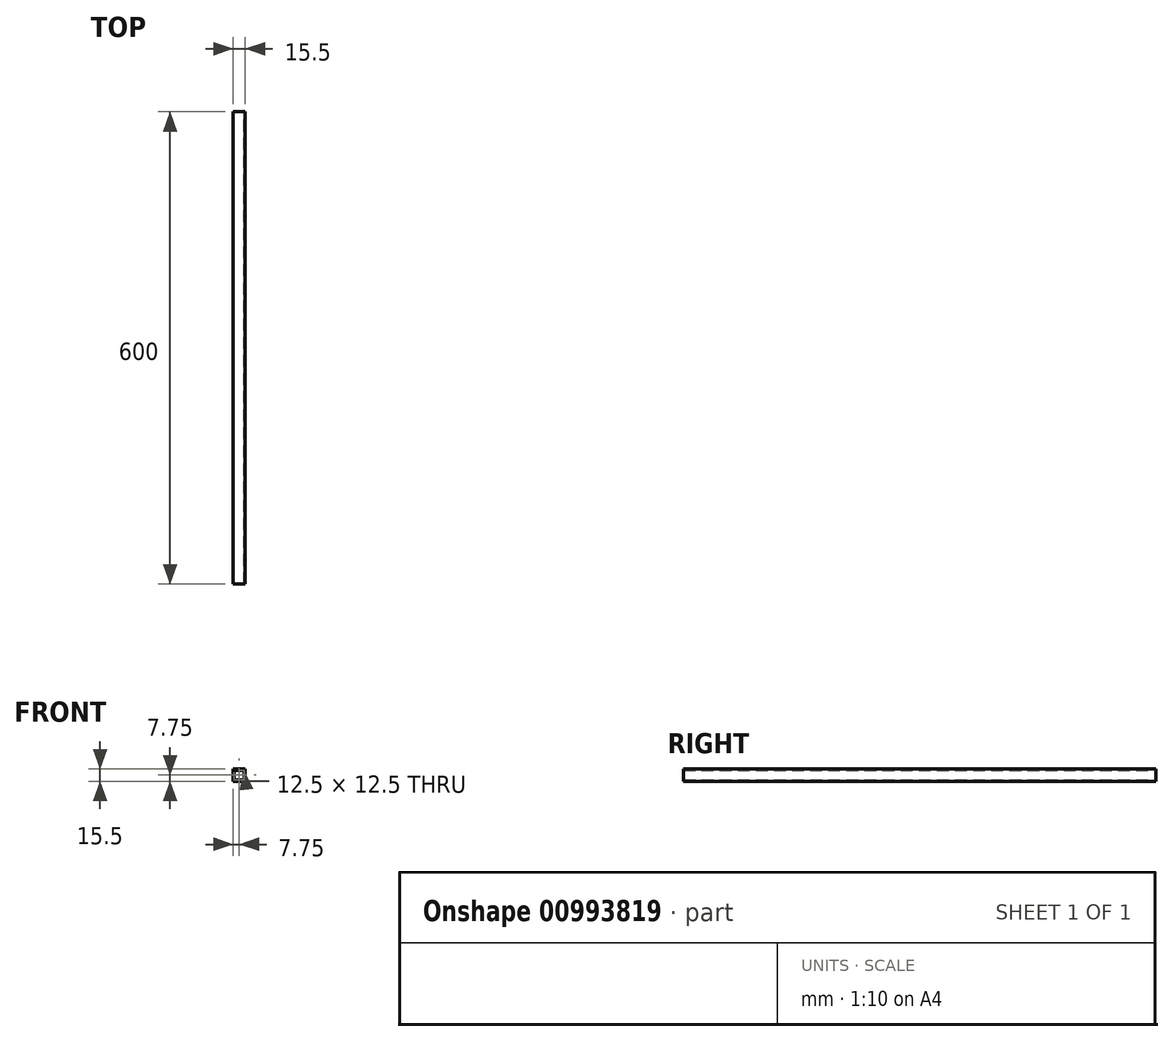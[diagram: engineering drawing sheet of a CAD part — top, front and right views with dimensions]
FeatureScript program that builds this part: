
annotation { "Feature Type Name" : "Feature", "Feature Type Description" : "" }
export const myFeature = defineFeature(function(context is Context, id is Id, definition is map)
    precondition{}
    {
        {
            var Q0;
            Q0=qCreatedBy(makeId("Front.planeOp"),FACE);
            var sketch = newSketch(context, id + "F0", { "sketchPlane" : qUnion([Q0])});
            skLineSegment(sketch, "E0.bottom", {"start": v(7.75, 7.75) * mm, "end": v(-7.75, 7.75) * mm});
            skLineSegment(sketch, "E0.top", {"start": v(7.75, -7.75) * mm, "end": v(-7.75, -7.75) * mm});
            skLineSegment(sketch, "E0.left", {"start": v(7.75, 7.75) * mm, "end": v(7.75, -7.75) * mm});
            skLineSegment(sketch, "E0.right", {"start": v(-7.75, 7.75) * mm, "end": v(-7.75, -7.75) * mm});
            skPoint(sketch, "E0.middle", {"position": v(0, 0) * mm});
            skLineSegment(sketch, "E1.bottom", {"start": v(6.25, 6.25) * mm, "end": v(-6.25, 6.25) * mm});
            skLineSegment(sketch, "E1.top", {"start": v(6.25, -6.25) * mm, "end": v(-6.25, -6.25) * mm});
            skLineSegment(sketch, "E1.left", {"start": v(6.25, 6.25) * mm, "end": v(6.25, -6.25) * mm});
            skLineSegment(sketch, "E1.right", {"start": v(-6.25, 6.25) * mm, "end": v(-6.25, -6.25) * mm});
            skSolve(sketch);
        }
        {
            var Q0;
            Q0=makeQuery(id+"F0.imprint","IMPRINT",FACE,{"disambiguationData":[TD([[makeQuery(id+"F0.imprint","IMPRINT",EDGE,{"derivedFrom":sQuery(id+"F0.wireOp",EDGE,"E0.bottom")}),1.0]])]});
            extrude(context, id + "F1", {"entities" : qUnion([Q0]), "depth" : 600 * mm, "offsetDistance" : 25 * mm, "symmetric" : true});
        }
    });
